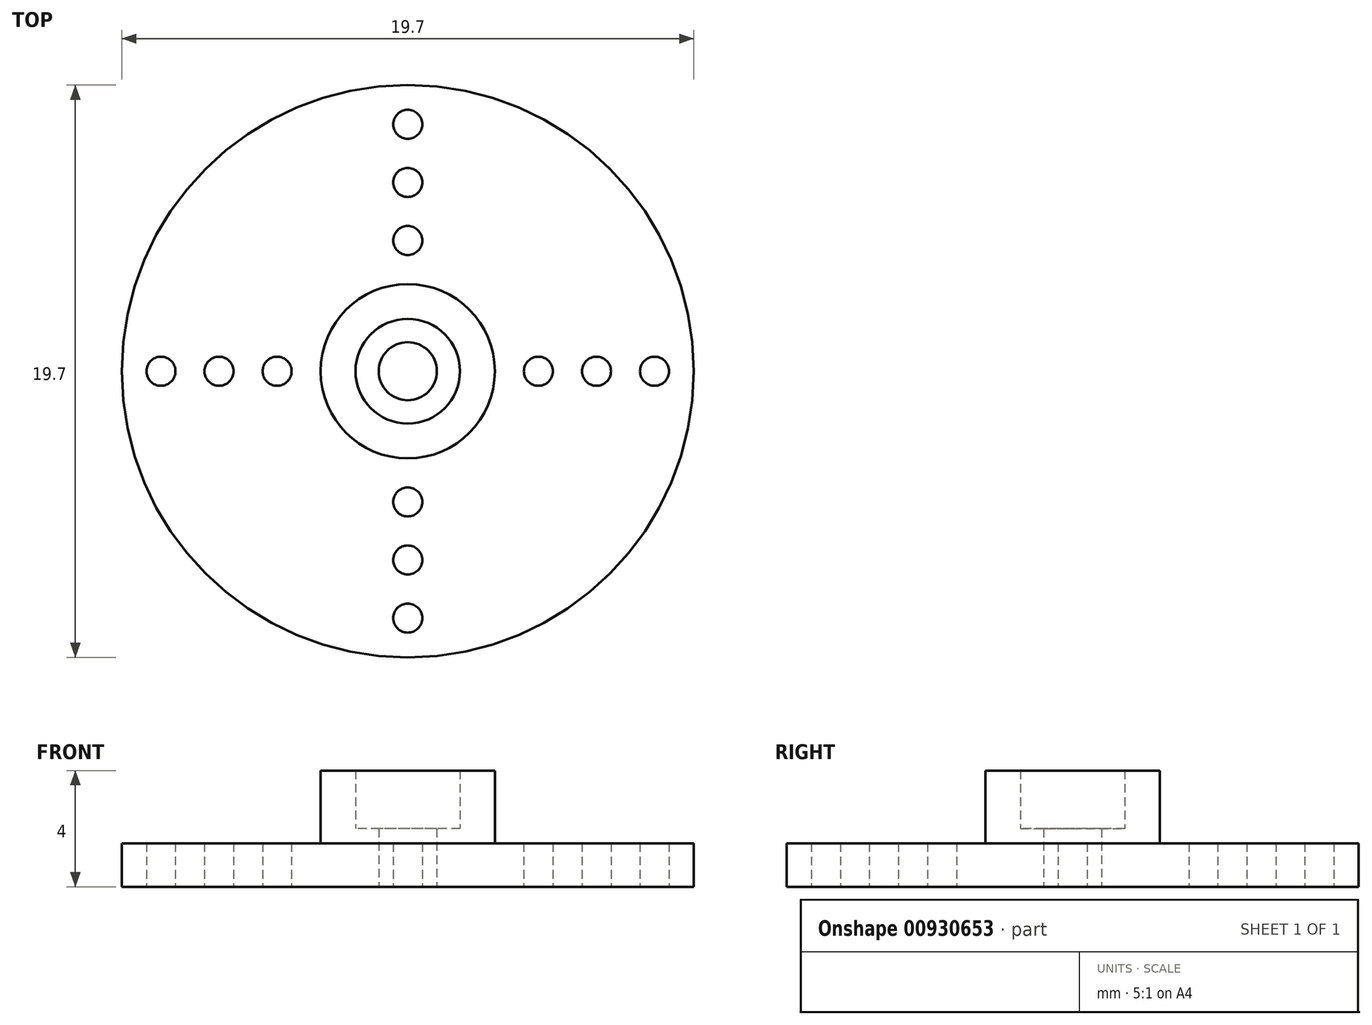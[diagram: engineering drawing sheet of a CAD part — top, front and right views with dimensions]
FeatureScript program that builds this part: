
annotation { "Feature Type Name" : "Feature", "Feature Type Description" : "" }
export const myFeature = defineFeature(function(context is Context, id is Id, definition is map)
    precondition{}
    {
        {
            var Q0;
            Q0=qCreatedBy(makeId("Top.planeOp"),FACE);
            var sketch = newSketch(context, id + "F0", { "sketchPlane" : qUnion([Q0])});
            skCircle(sketch, "E0", {"center": v(0, 0) * mm, "radius": 9.85 * mm});
            skCircle(sketch, "E1", {"center": v(-8.5, 0) * mm, "radius": 0.5 * mm});
            skCircle(sketch, "E2", {"center": v(-6.5, 0) * mm, "radius": 0.5 * mm});
            skCircle(sketch, "E3", {"center": v(-4.5, 0) * mm, "radius": 0.5 * mm});
            skCircle(sketch, "E4", {"center": v(4.5, 0) * mm, "radius": 0.5 * mm});
            skCircle(sketch, "E5", {"center": v(6.5, 0) * mm, "radius": 0.5 * mm});
            skCircle(sketch, "E6", {"center": v(8.5, 0) * mm, "radius": 0.5 * mm});
            skCircle(sketch, "E7", {"center": v(0, 4.5) * mm, "radius": 0.5 * mm});
            skCircle(sketch, "E8", {"center": v(0, 6.5) * mm, "radius": 0.5 * mm});
            skCircle(sketch, "E9", {"center": v(0, 8.5) * mm, "radius": 0.5 * mm});
            skCircle(sketch, "E10", {"center": v(0, -4.5) * mm, "radius": 0.5 * mm});
            skCircle(sketch, "E11", {"center": v(0, -6.5) * mm, "radius": 0.5 * mm});
            skCircle(sketch, "E12", {"center": v(0, -8.5) * mm, "radius": 0.5 * mm});
            skCircle(sketch, "E13", {"center": v(0, 0) * mm, "radius": 1 * mm});
            skSolve(sketch);
        }
        {
            var Q0;
            Q0=qSketchRegion(id+"F0",true);
            extrude(context, id + "F1", {"entities" : qUnion([Q0]), "depth" : 1.5 * mm, "offsetDistance" : 25 * mm});
        }
        {
            var Q0;
            Q0=makeQuery(id+"F1.opExtrude","CAP_FACE",FACE,{"disambiguationData":[OSD([sQuery(id+"F0.wireOp",EDGE,"E0"),sQuery(id+"F0.wireOp",EDGE,"E1"),sQuery(id+"F0.wireOp",EDGE,"E2"),sQuery(id+"F0.wireOp",EDGE,"E3"),sQuery(id+"F0.wireOp",EDGE,"E4"),sQuery(id+"F0.wireOp",EDGE,"E5"),sQuery(id+"F0.wireOp",EDGE,"E6"),sQuery(id+"F0.wireOp",EDGE,"E7"),sQuery(id+"F0.wireOp",EDGE,"E8"),sQuery(id+"F0.wireOp",EDGE,"E9"),sQuery(id+"F0.wireOp",EDGE,"E10"),sQuery(id+"F0.wireOp",EDGE,"E11"),sQuery(id+"F0.wireOp",EDGE,"E12"),sQuery(id+"F0.wireOp",EDGE,"E13")])],"isStart":false});
            var sketch = newSketch(context, id + "F2", { "sketchPlane" : qUnion([Q0])});
            skCircle(sketch, "E14", {"center": v(0, 0) * mm, "radius": 3 * mm});
            skCircle(sketch, "E15", {"center": v(0, 0) * mm, "radius": 1.8 * mm});
            skSolve(sketch);
        }
        {
            var Q0;
            Q0=qSketchRegion(id+"F2",true);
            extrude(context, id + "F3", {"entities" : qUnion([Q0]), "operationType" : NewBodyOperationType.ADD, "depth" : 2.5 * mm, "offsetDistance" : 25 * mm});
        }
        {
            var Q0;
            {var subQ0=sQuery(id+"F0.wireOp",EDGE,"E13");Q0=makeQuery(id+"F3.boolean.opBoolean","SPLIT",FACE,{"disambiguationData":[TD([makeQuery(id+"F1.opExtrude","SWEPT_FACE",FACE,{"disambiguationData":[OSD([subQ0])]})])],"derivedFrom":makeQuery(id+"F1.opExtrude","CAP_FACE",FACE,{"disambiguationData":[OSD([sQuery(id+"F0.wireOp",EDGE,"E0"),sQuery(id+"F0.wireOp",EDGE,"E1"),sQuery(id+"F0.wireOp",EDGE,"E2"),sQuery(id+"F0.wireOp",EDGE,"E3"),sQuery(id+"F0.wireOp",EDGE,"E4"),sQuery(id+"F0.wireOp",EDGE,"E5"),sQuery(id+"F0.wireOp",EDGE,"E6"),sQuery(id+"F0.wireOp",EDGE,"E7"),sQuery(id+"F0.wireOp",EDGE,"E8"),sQuery(id+"F0.wireOp",EDGE,"E9"),sQuery(id+"F0.wireOp",EDGE,"E10"),sQuery(id+"F0.wireOp",EDGE,"E11"),sQuery(id+"F0.wireOp",EDGE,"E12"),subQ0])],"isStart":false})});}
            var sketch = newSketch(context, id + "F4", { "sketchPlane" : qUnion([Q0])});
            skCircle(sketch, "E16", {"center": v(0, 0) * mm, "radius": 1 * mm});
            skCircle(sketch, "E17", {"center": v(0, 0) * mm, "radius": 1.8 * mm});
            skSolve(sketch);
        }
        {
            var Q0;
            Q0=qSketchRegion(id+"F4",true);
            extrude(context, id + "F5", {"entities" : qUnion([Q0]), "operationType" : NewBodyOperationType.ADD, "depth" : 0.5 * mm, "offsetDistance" : 25 * mm});
        }
    });
